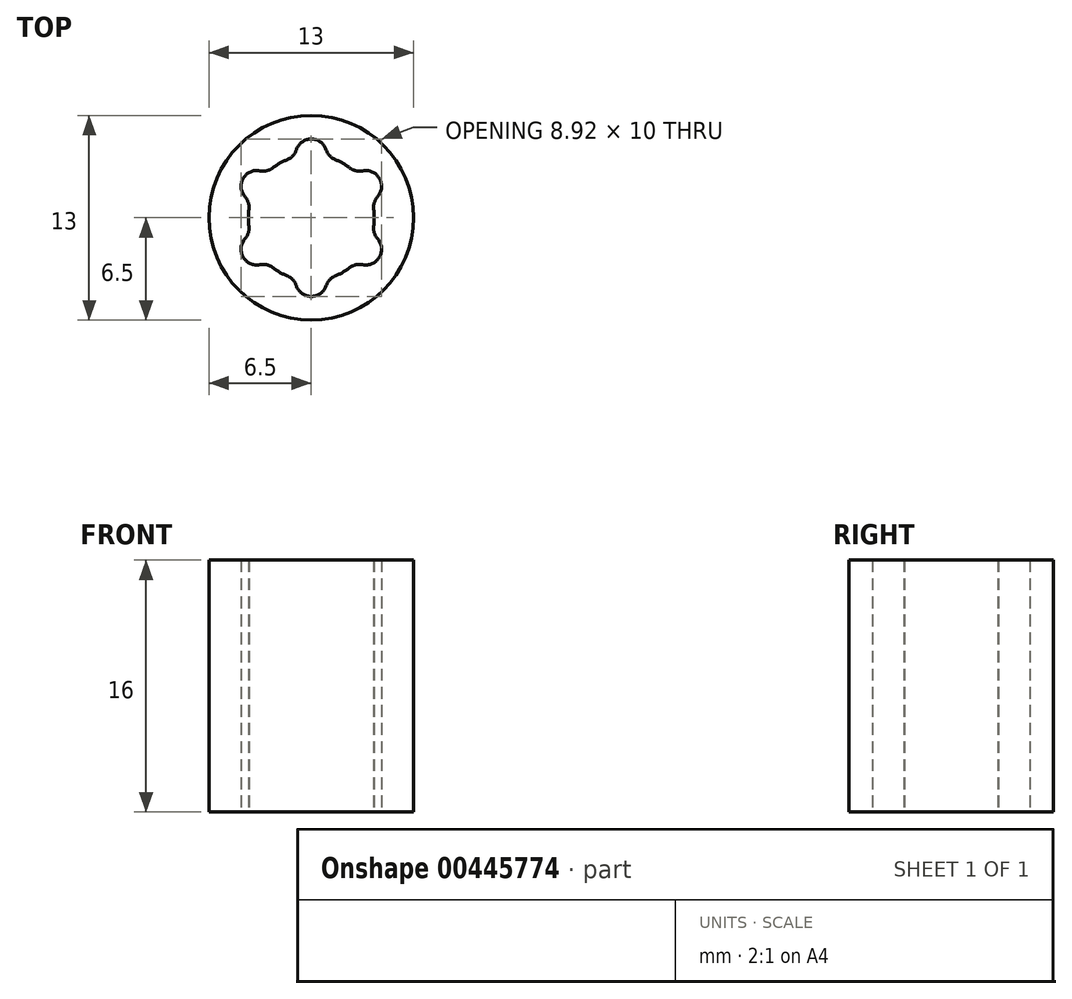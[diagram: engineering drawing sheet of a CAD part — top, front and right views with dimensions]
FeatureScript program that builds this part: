
annotation { "Feature Type Name" : "Feature", "Feature Type Description" : "" }
export const myFeature = defineFeature(function(context is Context, id is Id, definition is map)
    precondition{}
    {
        {
            var Q0;
            Q0=qCreatedBy(makeId("Top.planeOp"),FACE);
            var sketch = newSketch(context, id + "F0", { "sketchPlane" : qUnion([Q0])});
            skCircle(sketch, "E0", {"center": v(0, 0) * mm, "radius": 4 * mm});
            skCircle(sketch, "E1", {"center": v(0, 0) * mm, "radius": 6.5 * mm});
            skCircle(sketch, "E2", {"center": v(0, 4) * mm, "radius": 1 * mm});
            skLineSegment(sketch, "E3", {"start": v(0, 0) * mm, "end": v(0, 6.5) * mm, "construction": true});
            skSolve(sketch);
        }
        {
            var Q0;
            Q0 = qSketchRegion(id + "F0", true);
            var Q1;
            {var subQ0=sQuery(id+"F0.wireOp",EDGE,"E2");var subQ1=sQuery(id+"F0.wireOp",EDGE,"E0");var subQ2=makeQuery(id+"F0.imprint","INTERSECT",VERTEX,{"disambiguationData":[OD(0.0)],"derivedFrom":[subQ1,subQ0]});Q1=makeQuery(id+"F0.imprint","IMPRINT",FACE,{"disambiguationData":[TD([[makeQuery(id+"F0.imprint","IMPRINT",EDGE,{"disambiguationData":[TD([[subQ2,1.0]])],"derivedFrom":subQ1}),-1.0]])]});}
            extrude(context, id + "F1", {"entities" : qUnion([Q0, Q1]), "depth" : 16 * mm, "offsetDistance" : 25 * mm});
        }
        {
            var Q0;
            {var subQ0=sQuery(id+"F0.wireOp",EDGE,"E2");var subQ1=sQuery(id+"F0.wireOp",EDGE,"E0");var subQ2=makeQuery(id+"F0.imprint","INTERSECT",VERTEX,{"disambiguationData":[OD(0.0)],"derivedFrom":[subQ1,subQ0]});Q0=makeQuery(id+"F0.imprint","IMPRINT",FACE,{"disambiguationData":[TD([[makeQuery(id+"F0.imprint","IMPRINT",EDGE,{"disambiguationData":[TD([[subQ2,1.0]])],"derivedFrom":subQ1}),1.0]])]});}
            var Q1;
            {var subQ0=sQuery(id+"F0.wireOp",EDGE,"E2");var subQ1=sQuery(id+"F0.wireOp",EDGE,"E0");var subQ2=makeQuery(id+"F0.imprint","INTERSECT",VERTEX,{"disambiguationData":[OD(0.0)],"derivedFrom":[subQ1,subQ0]});Q1=makeQuery(id+"F0.imprint","IMPRINT",FACE,{"disambiguationData":[TD([[makeQuery(id+"F0.imprint","IMPRINT",EDGE,{"disambiguationData":[TD([[subQ2,1.0]])],"derivedFrom":subQ1}),-1.0]])]});}
            var Q2;
            Q2=makeQuery(id+"F1.opExtrude","CAP_FACE",FACE,{"disambiguationData":[OSD([sQuery(id+"F0.wireOp",EDGE,"E0"),sQuery(id+"F0.wireOp",EDGE,"E1")])],"isStart":false});
            extrude(context, id + "F2", {"entities" : qUnion([Q0, Q1]), "endBound" : BoundingType.UP_TO_SURFACE, "depth" : 25 * mm, "endBoundEntityFace" : qUnion([Q2]), "offsetDistance" : 25 * mm});
        }
        {
            var Q0;
            Q0=qCreatedBy(makeId("Right.planeOp"),FACE);
            var sketch = newSketch(context, id + "F3", { "sketchPlane" : qUnion([Q0])});
            skLineSegment(sketch, "E4", {"start": v(0, 28.57) * mm, "end": v(0, -22.1) * mm, "construction": true});
            skSolve(sketch);
        }
        {
            var Q0;
            Q0=makeQuery(id+"F2.opExtrude","SWEPT_BODY",BODY,{"disambiguationData":[OSD([sQuery(id+"F0.wireOp",EDGE,"E2")])]});
            var Q1;
            Q1=sQuery(id+"F3.wireOp",EDGE,"E4");
            circularPattern(context, id + "F4", {"operationType" : NewBodyOperationType.REMOVE, "entities" : qUnion([Q0]), "axis" : qUnion([Q1]), "angle" : 360 * degree, "instanceCount" : 6, "equalSpace" : true});
        }
        {
            var Q0;
            Q0=makeQuery(id+"F4.boolean.opBoolean","INTERSECT",EDGE,{"disambiguationData":[OD(0.0)],"derivedFrom":[makeQuery(id+"F1.opExtrude","SWEPT_FACE",FACE,{"disambiguationData":[OSD([sQuery(id+"F0.wireOp",EDGE,"E0")])]}),makeQuery(id+"F4.opPattern","COPY",FACE,{"derivedFrom":makeQuery(id+"F2.opExtrude","SWEPT_FACE",FACE,{"disambiguationData":[OSD([sQuery(id+"F0.wireOp",EDGE,"E2")])]}),"instanceName":"4"})]});
            var Q1;
            Q1=makeQuery(id+"F4.boolean.opBoolean","INTERSECT",EDGE,{"disambiguationData":[OD(1.0)],"derivedFrom":[makeQuery(id+"F1.opExtrude","SWEPT_FACE",FACE,{"disambiguationData":[OSD([sQuery(id+"F0.wireOp",EDGE,"E0")])]}),makeQuery(id+"F4.opPattern","COPY",FACE,{"derivedFrom":makeQuery(id+"F2.opExtrude","SWEPT_FACE",FACE,{"disambiguationData":[OSD([sQuery(id+"F0.wireOp",EDGE,"E2")])]}),"instanceName":"3"})]});
            var Q2;
            Q2=makeQuery(id+"F4.boolean.opBoolean","INTERSECT",EDGE,{"disambiguationData":[OD(1.0)],"derivedFrom":[makeQuery(id+"F1.opExtrude","SWEPT_FACE",FACE,{"disambiguationData":[OSD([sQuery(id+"F0.wireOp",EDGE,"E0")])]}),makeQuery(id+"F4.opPattern","COPY",FACE,{"derivedFrom":makeQuery(id+"F2.opExtrude","SWEPT_FACE",FACE,{"disambiguationData":[OSD([sQuery(id+"F0.wireOp",EDGE,"E2")])]}),"instanceName":"2"})]});
            var Q3;
            Q3=makeQuery(id+"F4.boolean.opBoolean","INTERSECT",EDGE,{"disambiguationData":[OD(0.0)],"derivedFrom":[makeQuery(id+"F1.opExtrude","SWEPT_FACE",FACE,{"disambiguationData":[OSD([sQuery(id+"F0.wireOp",EDGE,"E0")])]}),makeQuery(id+"F4.opPattern","COPY",FACE,{"derivedFrom":makeQuery(id+"F2.opExtrude","SWEPT_FACE",FACE,{"disambiguationData":[OSD([sQuery(id+"F0.wireOp",EDGE,"E2")])]}),"instanceName":"3"})]});
            var Q4;
            Q4=makeQuery(id+"F4.boolean.opBoolean","INTERSECT",EDGE,{"disambiguationData":[OD(0.0)],"derivedFrom":[makeQuery(id+"F1.opExtrude","SWEPT_FACE",FACE,{"disambiguationData":[OSD([sQuery(id+"F0.wireOp",EDGE,"E0")])]}),makeQuery(id+"F4.opPattern","COPY",FACE,{"derivedFrom":makeQuery(id+"F2.opExtrude","SWEPT_FACE",FACE,{"disambiguationData":[OSD([sQuery(id+"F0.wireOp",EDGE,"E2")])]}),"instanceName":"2"})]});
            var Q5;
            Q5=makeQuery(id+"F4.boolean.opBoolean","INTERSECT",EDGE,{"disambiguationData":[OD(1.0)],"derivedFrom":[makeQuery(id+"F1.opExtrude","SWEPT_FACE",FACE,{"disambiguationData":[OSD([sQuery(id+"F0.wireOp",EDGE,"E0")])]}),makeQuery(id+"F4.opPattern","COPY",FACE,{"derivedFrom":makeQuery(id+"F2.opExtrude","SWEPT_FACE",FACE,{"disambiguationData":[OSD([sQuery(id+"F0.wireOp",EDGE,"E2")])]}),"instanceName":"1"})]});
            var Q6;
            Q6=makeQuery(id+"F4.boolean.opBoolean","INTERSECT",EDGE,{"disambiguationData":[OD(0.0)],"derivedFrom":[makeQuery(id+"F1.opExtrude","SWEPT_FACE",FACE,{"disambiguationData":[OSD([sQuery(id+"F0.wireOp",EDGE,"E0")])]}),makeQuery(id+"F4.opPattern","COPY",FACE,{"derivedFrom":makeQuery(id+"F2.opExtrude","SWEPT_FACE",FACE,{"disambiguationData":[OSD([sQuery(id+"F0.wireOp",EDGE,"E2")])]}),"instanceName":"1"})]});
            var Q7;
            Q7=makeQuery(id+"F4.boolean.opBoolean","INTERSECT",EDGE,{"disambiguationData":[OD(0.0)],"derivedFrom":[makeQuery(id+"F1.opExtrude","SWEPT_FACE",FACE,{"disambiguationData":[OSD([sQuery(id+"F0.wireOp",EDGE,"E0")])]}),makeQuery(id+"F2.opExtrude","SWEPT_FACE",FACE,{"disambiguationData":[OSD([sQuery(id+"F0.wireOp",EDGE,"E2")])]})]});
            var Q8;
            Q8=makeQuery(id+"F4.boolean.opBoolean","INTERSECT",EDGE,{"disambiguationData":[OD(1.0)],"derivedFrom":[makeQuery(id+"F1.opExtrude","SWEPT_FACE",FACE,{"disambiguationData":[OSD([sQuery(id+"F0.wireOp",EDGE,"E0")])]}),makeQuery(id+"F2.opExtrude","SWEPT_FACE",FACE,{"disambiguationData":[OSD([sQuery(id+"F0.wireOp",EDGE,"E2")])]})]});
            var Q9;
            Q9=makeQuery(id+"F4.boolean.opBoolean","INTERSECT",EDGE,{"disambiguationData":[OD(0.0)],"derivedFrom":[makeQuery(id+"F1.opExtrude","SWEPT_FACE",FACE,{"disambiguationData":[OSD([sQuery(id+"F0.wireOp",EDGE,"E0")])]}),makeQuery(id+"F4.opPattern","COPY",FACE,{"derivedFrom":makeQuery(id+"F2.opExtrude","SWEPT_FACE",FACE,{"disambiguationData":[OSD([sQuery(id+"F0.wireOp",EDGE,"E2")])]}),"instanceName":"5"})]});
            var Q10;
            Q10=makeQuery(id+"F4.boolean.opBoolean","INTERSECT",EDGE,{"disambiguationData":[OD(1.0)],"derivedFrom":[makeQuery(id+"F1.opExtrude","SWEPT_FACE",FACE,{"disambiguationData":[OSD([sQuery(id+"F0.wireOp",EDGE,"E0")])]}),makeQuery(id+"F4.opPattern","COPY",FACE,{"derivedFrom":makeQuery(id+"F2.opExtrude","SWEPT_FACE",FACE,{"disambiguationData":[OSD([sQuery(id+"F0.wireOp",EDGE,"E2")])]}),"instanceName":"5"})]});
            var Q11;
            Q11=makeQuery(id+"F4.boolean.opBoolean","INTERSECT",EDGE,{"disambiguationData":[OD(1.0)],"derivedFrom":[makeQuery(id+"F1.opExtrude","SWEPT_FACE",FACE,{"disambiguationData":[OSD([sQuery(id+"F0.wireOp",EDGE,"E0")])]}),makeQuery(id+"F4.opPattern","COPY",FACE,{"derivedFrom":makeQuery(id+"F2.opExtrude","SWEPT_FACE",FACE,{"disambiguationData":[OSD([sQuery(id+"F0.wireOp",EDGE,"E2")])]}),"instanceName":"4"})]});
            fillet(context, id + "F5", {"entities" : qUnion([Q0, Q1, Q2, Q3, Q4, Q5, Q6, Q7, Q8, Q9, Q10, Q11]), "radius" : 1 * mm, "tangentPropagation" : true, "allowEdgeOverflow" : false});
        }
    });
